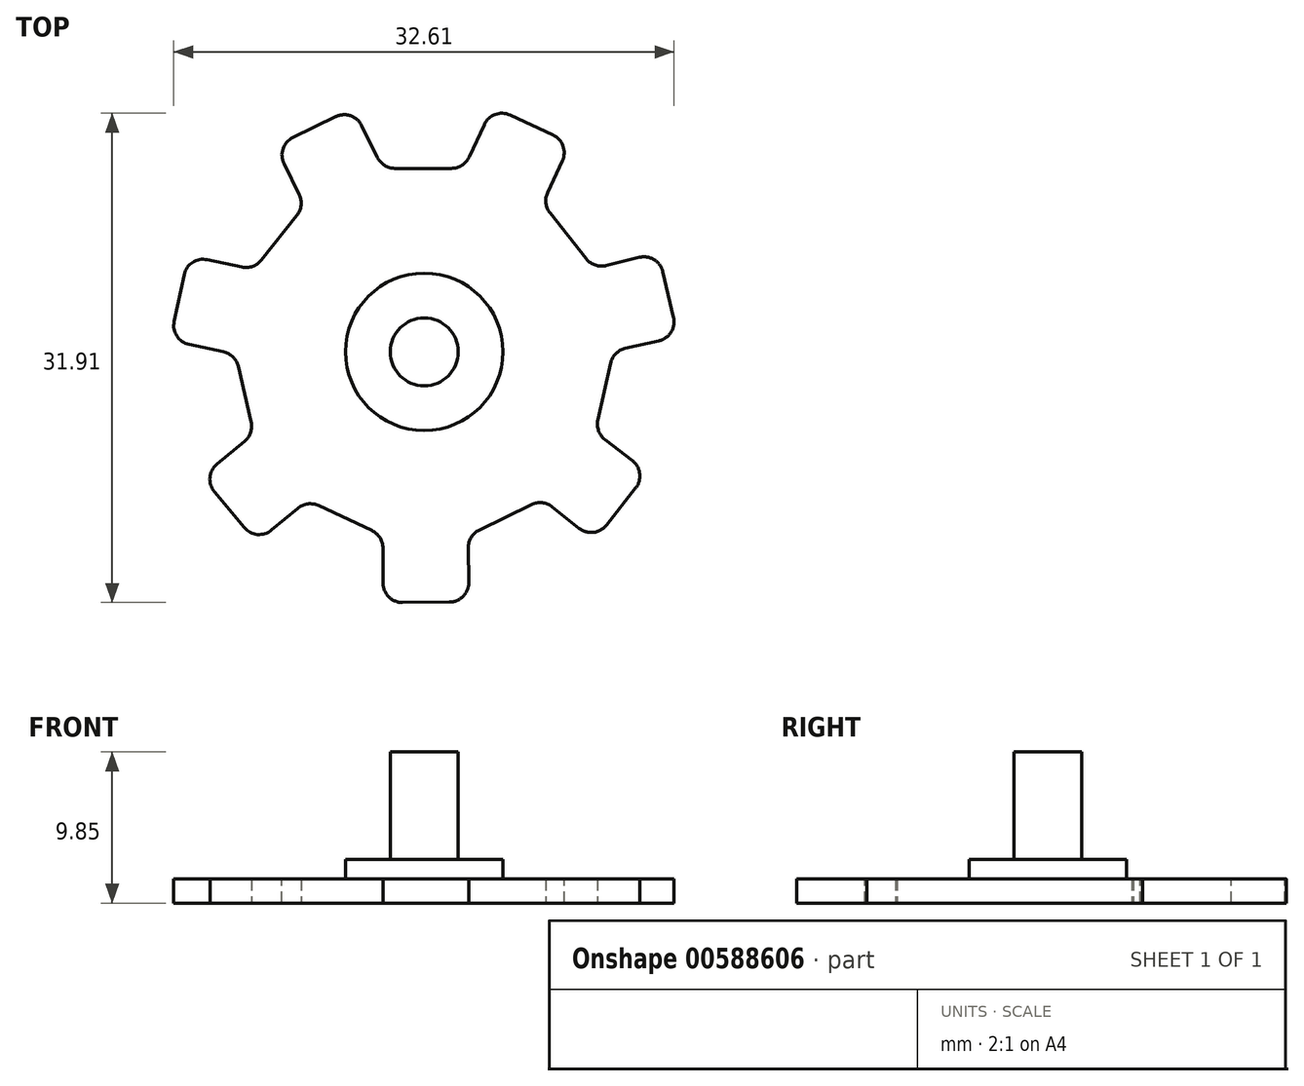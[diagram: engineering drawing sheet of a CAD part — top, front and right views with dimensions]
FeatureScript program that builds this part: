
annotation { "Feature Type Name" : "Feature", "Feature Type Description" : "" }
export const myFeature = defineFeature(function(context is Context, id is Id, definition is map)
    precondition{}
    {
        {
            var Q0;
            Q0=qCreatedBy(makeId("Top.planeOp"),FACE);
            var sketch = newSketch(context, id + "F0", { "sketchPlane" : qUnion([Q0])});
            skLineSegment(sketch, "E0", {"start": v(-2.4, 14.6) * mm, "end": v(-2.4, 10.7) * mm});
            skLineSegment(sketch, "E1", {"start": v(-2.4, 10.7) * mm, "end": v(-6.8, 8.65) * mm});
            skLineSegment(sketch, "E2", {"start": v(-6.8, 8.65) * mm, "end": v(-9.75, 11.1) * mm});
            skLineSegment(sketch, "E3", {"start": v(-9.75, 11.1) * mm, "end": v(-12.94, 7.27) * mm});
            skLineSegment(sketch, "E4", {"start": v(-12.94, 7.27) * mm, "end": v(-9.92, 4.76) * mm});
            skLineSegment(sketch, "E5", {"start": v(-9.92, 4.76) * mm, "end": v(-10.99, 0.15) * mm});
            skLineSegment(sketch, "E6", {"start": v(-10.99, 0.15) * mm, "end": v(-14.79, -0.67) * mm});
            skLineSegment(sketch, "E7", {"start": v(-14.79, -0.67) * mm, "end": v(-13.73, -5.6) * mm});
            skLineSegment(sketch, "E8", {"start": v(-13.73, -5.6) * mm, "end": v(-9.92, -4.78) * mm});
            skLineSegment(sketch, "E9", {"start": v(-9.92, -4.78) * mm, "end": v(-6.97, -8.51) * mm});
            skLineSegment(sketch, "E10", {"start": v(-6.97, -8.51) * mm, "end": v(-8.66, -11.97) * mm});
            skLineSegment(sketch, "E11", {"start": v(-8.66, -11.97) * mm, "end": v(-4.14, -14.2) * mm});
            skLineSegment(sketch, "E12", {"start": v(-4.14, -14.2) * mm, "end": v(-2.42, -10.68) * mm});
            skLineSegment(sketch, "E13", {"start": v(-2.42, -10.68) * mm, "end": v(2.3, -10.68) * mm});
            skLineSegment(sketch, "E14", {"start": v(2.3, -10.68) * mm, "end": v(3.97, -14.26) * mm});
            skLineSegment(sketch, "E15", {"start": v(3.97, -14.26) * mm, "end": v(8.52, -12.15) * mm});
            skLineSegment(sketch, "E16", {"start": v(8.52, -12.15) * mm, "end": v(6.88, -8.63) * mm});
            skLineSegment(sketch, "E17", {"start": v(6.88, -8.63) * mm, "end": v(9.89, -4.84) * mm});
            skLineSegment(sketch, "E18", {"start": v(9.89, -4.84) * mm, "end": v(13.62, -5.78) * mm});
            skLineSegment(sketch, "E19", {"start": v(13.62, -5.78) * mm, "end": v(14.77, -0.9) * mm});
            skLineSegment(sketch, "E20", {"start": v(14.77, -0.9) * mm, "end": v(11, -0.04) * mm});
            skLineSegment(sketch, "E21", {"start": v(11, -0.04) * mm, "end": v(9.95, 4.67) * mm});
            skLineSegment(sketch, "E22", {"start": v(9.95, 4.67) * mm, "end": v(13, 7.03) * mm});
            skLineSegment(sketch, "E23", {"start": v(13, 7.03) * mm, "end": v(9.9, 10.98) * mm});
            skLineSegment(sketch, "E24", {"start": v(9.9, 10.98) * mm, "end": v(6.88, 8.58) * mm});
            skLineSegment(sketch, "E25", {"start": v(6.88, 8.58) * mm, "end": v(2.55, 10.7) * mm});
            skLineSegment(sketch, "E26", {"start": v(2.55, 10.7) * mm, "end": v(2.6, 14.56) * mm});
            skLineSegment(sketch, "E27", {"start": v(2.6, 14.56) * mm, "end": v(-2.4, 14.6) * mm});
            skSolve(sketch);
        }
        {
            var Q0;
            Q0=qSketchRegion(id+"F0",true);
            extrude(context, id + "F1", {"entities" : qUnion([Q0]), "depth" : 2.54 * mm, "offsetDistance" : 25.4 * mm});
        }
        {
            var Q0;
            Q0=makeQuery(id+"F1.opExtrude","SWEPT_BODY",BODY,{"disambiguationData":[OSD([sQuery(id+"F0.wireOp",EDGE,"E0"),sQuery(id+"F0.wireOp",EDGE,"E1"),sQuery(id+"F0.wireOp",EDGE,"E2"),sQuery(id+"F0.wireOp",EDGE,"E3"),sQuery(id+"F0.wireOp",EDGE,"E4"),sQuery(id+"F0.wireOp",EDGE,"E5"),sQuery(id+"F0.wireOp",EDGE,"E6"),sQuery(id+"F0.wireOp",EDGE,"E7"),sQuery(id+"F0.wireOp",EDGE,"E8"),sQuery(id+"F0.wireOp",EDGE,"E9"),sQuery(id+"F0.wireOp",EDGE,"E10"),sQuery(id+"F0.wireOp",EDGE,"E11"),sQuery(id+"F0.wireOp",EDGE,"E12"),sQuery(id+"F0.wireOp",EDGE,"E13"),sQuery(id+"F0.wireOp",EDGE,"E14"),sQuery(id+"F0.wireOp",EDGE,"E15"),sQuery(id+"F0.wireOp",EDGE,"E16"),sQuery(id+"F0.wireOp",EDGE,"E17"),sQuery(id+"F0.wireOp",EDGE,"E18"),sQuery(id+"F0.wireOp",EDGE,"E19"),sQuery(id+"F0.wireOp",EDGE,"E20"),sQuery(id+"F0.wireOp",EDGE,"E21"),sQuery(id+"F0.wireOp",EDGE,"E22"),sQuery(id+"F0.wireOp",EDGE,"E23"),sQuery(id+"F0.wireOp",EDGE,"E24"),sQuery(id+"F0.wireOp",EDGE,"E25"),sQuery(id+"F0.wireOp",EDGE,"E26"),sQuery(id+"F0.wireOp",EDGE,"E27")])]});
            var Q1;
            Q1=qCreatedBy(makeId("Origin.pointOp"),VERTEX);
            transform(context, id + "F2", {"entities" : qUnion([Q0]), "transformType" : TransformType.SCALE_UNIFORMLY, "scale" : 1.12, "scalePoint" : qUnion([Q1]), "makeCopy" : false});
        }
        {
            var Q0;
            Q0=makeQuery(id+"F1.opExtrude","SWEPT_EDGE",EDGE,{"disambiguationData":[OSD([sQuery(id+"F0.wireOp",EDGE,"E6"),sQuery(id+"F0.wireOp",EDGE,"E7")])]});
            var Q1;
            Q1=makeQuery(id+"F1.opExtrude","SWEPT_EDGE",EDGE,{"disambiguationData":[OSD([sQuery(id+"F0.wireOp",EDGE,"E5"),sQuery(id+"F0.wireOp",EDGE,"E6")])]});
            var Q2;
            {var subQ0=sQuery(id+"F0.wireOp",EDGE,"E4");Q2=makeQuery(id+"Fj5wciNK8VLjmr4_1.opFillet","BLEND_EDGE",EDGE,{"blendedFrom":[makeQuery(id+"F1.opExtrude","CAP_EDGE",EDGE,{"disambiguationData":[OSD([subQ0])],"isStart":false}),makeQuery(id+"F1.opExtrude","SWEPT_FACE",FACE,{"disambiguationData":[OSD([subQ0])]})],"blendedInto":[makeQuery(id+"F1.opExtrude","SWEPT_FACE",FACE,{"disambiguationData":[OSD([subQ0])]})]});}
            var Q3;
            Q3=makeQuery(id+"F1.opExtrude","SWEPT_EDGE",EDGE,{"disambiguationData":[OSD([sQuery(id+"F0.wireOp",EDGE,"E3"),sQuery(id+"F0.wireOp",EDGE,"E4")])]});
            var Q4;
            Q4=makeQuery(id+"F1.opExtrude","SWEPT_EDGE",EDGE,{"disambiguationData":[OSD([sQuery(id+"F0.wireOp",EDGE,"E2"),sQuery(id+"F0.wireOp",EDGE,"E3")])]});
            var Q5;
            Q5=makeQuery(id+"F1.opExtrude","SWEPT_EDGE",EDGE,{"disambiguationData":[OSD([sQuery(id+"F0.wireOp",EDGE,"E1"),sQuery(id+"F0.wireOp",EDGE,"E2")])]});
            var Q6;
            Q6=makeQuery(id+"F1.opExtrude","SWEPT_EDGE",EDGE,{"disambiguationData":[OSD([sQuery(id+"F0.wireOp",EDGE,"E0"),sQuery(id+"F0.wireOp",EDGE,"E1")])]});
            var Q7;
            Q7=makeQuery(id+"F1.opExtrude","SWEPT_EDGE",EDGE,{"disambiguationData":[OSD([sQuery(id+"F0.wireOp",EDGE,"E0"),sQuery(id+"F0.wireOp",EDGE,"E27")])]});
            var Q8;
            Q8=makeQuery(id+"F1.opExtrude","SWEPT_EDGE",EDGE,{"disambiguationData":[OSD([sQuery(id+"F0.wireOp",EDGE,"E26"),sQuery(id+"F0.wireOp",EDGE,"E27")])]});
            var Q9;
            Q9=makeQuery(id+"F1.opExtrude","SWEPT_EDGE",EDGE,{"disambiguationData":[OSD([sQuery(id+"F0.wireOp",EDGE,"E25"),sQuery(id+"F0.wireOp",EDGE,"E26")])]});
            var Q10;
            Q10=makeQuery(id+"F1.opExtrude","SWEPT_EDGE",EDGE,{"disambiguationData":[OSD([sQuery(id+"F0.wireOp",EDGE,"E24"),sQuery(id+"F0.wireOp",EDGE,"E25")])]});
            var Q11;
            Q11=makeQuery(id+"F1.opExtrude","SWEPT_EDGE",EDGE,{"disambiguationData":[OSD([sQuery(id+"F0.wireOp",EDGE,"E23"),sQuery(id+"F0.wireOp",EDGE,"E24")])]});
            var Q12;
            Q12=makeQuery(id+"F1.opExtrude","SWEPT_EDGE",EDGE,{"disambiguationData":[OSD([sQuery(id+"F0.wireOp",EDGE,"E22"),sQuery(id+"F0.wireOp",EDGE,"E23")])]});
            var Q13;
            Q13=makeQuery(id+"F1.opExtrude","SWEPT_EDGE",EDGE,{"disambiguationData":[OSD([sQuery(id+"F0.wireOp",EDGE,"E21"),sQuery(id+"F0.wireOp",EDGE,"E22")])]});
            var Q14;
            Q14=makeQuery(id+"F1.opExtrude","SWEPT_EDGE",EDGE,{"disambiguationData":[OSD([sQuery(id+"F0.wireOp",EDGE,"E20"),sQuery(id+"F0.wireOp",EDGE,"E21")])]});
            var Q15;
            Q15=makeQuery(id+"F1.opExtrude","SWEPT_EDGE",EDGE,{"disambiguationData":[OSD([sQuery(id+"F0.wireOp",EDGE,"E19"),sQuery(id+"F0.wireOp",EDGE,"E20")])]});
            var Q16;
            Q16=makeQuery(id+"F1.opExtrude","SWEPT_EDGE",EDGE,{"disambiguationData":[OSD([sQuery(id+"F0.wireOp",EDGE,"E18"),sQuery(id+"F0.wireOp",EDGE,"E19")])]});
            var Q17;
            Q17=makeQuery(id+"F1.opExtrude","SWEPT_EDGE",EDGE,{"disambiguationData":[OSD([sQuery(id+"F0.wireOp",EDGE,"E17"),sQuery(id+"F0.wireOp",EDGE,"E18")])]});
            var Q18;
            Q18=makeQuery(id+"F1.opExtrude","SWEPT_EDGE",EDGE,{"disambiguationData":[OSD([sQuery(id+"F0.wireOp",EDGE,"E16"),sQuery(id+"F0.wireOp",EDGE,"E17")])]});
            var Q19;
            Q19=makeQuery(id+"F1.opExtrude","SWEPT_EDGE",EDGE,{"disambiguationData":[OSD([sQuery(id+"F0.wireOp",EDGE,"E15"),sQuery(id+"F0.wireOp",EDGE,"E16")])]});
            var Q20;
            Q20=makeQuery(id+"F1.opExtrude","SWEPT_EDGE",EDGE,{"disambiguationData":[OSD([sQuery(id+"F0.wireOp",EDGE,"E14"),sQuery(id+"F0.wireOp",EDGE,"E15")])]});
            var Q21;
            Q21=makeQuery(id+"F1.opExtrude","SWEPT_EDGE",EDGE,{"disambiguationData":[OSD([sQuery(id+"F0.wireOp",EDGE,"E13"),sQuery(id+"F0.wireOp",EDGE,"E14")])]});
            var Q22;
            Q22=makeQuery(id+"F1.opExtrude","SWEPT_EDGE",EDGE,{"disambiguationData":[OSD([sQuery(id+"F0.wireOp",EDGE,"E12"),sQuery(id+"F0.wireOp",EDGE,"E13")])]});
            var Q23;
            Q23=makeQuery(id+"F1.opExtrude","SWEPT_EDGE",EDGE,{"disambiguationData":[OSD([sQuery(id+"F0.wireOp",EDGE,"E11"),sQuery(id+"F0.wireOp",EDGE,"E12")])]});
            var Q24;
            Q24=makeQuery(id+"F1.opExtrude","SWEPT_EDGE",EDGE,{"disambiguationData":[OSD([sQuery(id+"F0.wireOp",EDGE,"E10"),sQuery(id+"F0.wireOp",EDGE,"E11")])]});
            var Q25;
            Q25=makeQuery(id+"F1.opExtrude","SWEPT_EDGE",EDGE,{"disambiguationData":[OSD([sQuery(id+"F0.wireOp",EDGE,"E9"),sQuery(id+"F0.wireOp",EDGE,"E10")])]});
            var Q26;
            Q26=makeQuery(id+"F1.opExtrude","SWEPT_EDGE",EDGE,{"disambiguationData":[OSD([sQuery(id+"F0.wireOp",EDGE,"E8"),sQuery(id+"F0.wireOp",EDGE,"E9")])]});
            var Q27;
            Q27=makeQuery(id+"F1.opExtrude","SWEPT_EDGE",EDGE,{"disambiguationData":[OSD([sQuery(id+"F0.wireOp",EDGE,"E7"),sQuery(id+"F0.wireOp",EDGE,"E8")])]});
            var Q28;
            Q28=makeQuery(id+"F1.opExtrude","SWEPT_EDGE",EDGE,{"disambiguationData":[OSD([sQuery(id+"F0.wireOp",EDGE,"E4"),sQuery(id+"F0.wireOp",EDGE,"E5")])]});
            fillet(context, id + "F3", {"entities" : qUnion([Q0, Q1, Q2, Q3, Q4, Q5, Q6, Q7, Q8, Q9, Q10, Q11, Q12, Q13, Q14, Q15, Q16, Q17, Q18, Q19, Q20, Q21, Q22, Q23, Q24, Q25, Q26, Q27, Q28]), "radius" : 1.27 * mm, "tangentPropagation" : true, "allowEdgeOverflow" : false});
        }
        {
            var Q0;
            Q0=makeQuery(id+"F0.imprint","IMPRINT",FACE,{"disambiguationData":[TD([[makeQuery(id+"F0.imprint","IMPRINT",EDGE,{"derivedFrom":sQuery(id+"F0.wireOp",EDGE,"E0")}),1.0]])]});
            var sketch = newSketch(context, id + "F4", { "sketchPlane" : qUnion([Q0])});
            skCircle(sketch, "E28", {"center": v(0, 0) * mm, "radius": 2.2 * mm});
            skPoint(sketch, "E29.start.orphan", {"position": v(0, -2.2) * mm});
            skSolve(sketch);
        }
        {
            var Q0;
            Q0 = qSketchRegion(id + "F4", true);
            extrude(context, id + "F5", {"entities" : qUnion([Q0]), "operationType" : NewBodyOperationType.ADD, "oppositeDirection" : true, "depth" : 7 * mm, "offsetDistance" : 25.4 * mm});
        }
        {
            var Q0;
            Q0=makeQuery(id+"F1.opExtrude","SWEPT_BODY",BODY,{"disambiguationData":[OSD([sQuery(id+"F0.wireOp",EDGE,"E0"),sQuery(id+"F0.wireOp",EDGE,"E1"),sQuery(id+"F0.wireOp",EDGE,"E2"),sQuery(id+"F0.wireOp",EDGE,"E3"),sQuery(id+"F0.wireOp",EDGE,"E4"),sQuery(id+"F0.wireOp",EDGE,"E5"),sQuery(id+"F0.wireOp",EDGE,"E6"),sQuery(id+"F0.wireOp",EDGE,"E7"),sQuery(id+"F0.wireOp",EDGE,"E8"),sQuery(id+"F0.wireOp",EDGE,"E9"),sQuery(id+"F0.wireOp",EDGE,"E10"),sQuery(id+"F0.wireOp",EDGE,"E11"),sQuery(id+"F0.wireOp",EDGE,"E12"),sQuery(id+"F0.wireOp",EDGE,"E13"),sQuery(id+"F0.wireOp",EDGE,"E14"),sQuery(id+"F0.wireOp",EDGE,"E15"),sQuery(id+"F0.wireOp",EDGE,"E16"),sQuery(id+"F0.wireOp",EDGE,"E17"),sQuery(id+"F0.wireOp",EDGE,"E18"),sQuery(id+"F0.wireOp",EDGE,"E19"),sQuery(id+"F0.wireOp",EDGE,"E20"),sQuery(id+"F0.wireOp",EDGE,"E21"),sQuery(id+"F0.wireOp",EDGE,"E22"),sQuery(id+"F0.wireOp",EDGE,"E23"),sQuery(id+"F0.wireOp",EDGE,"E24"),sQuery(id+"F0.wireOp",EDGE,"E25"),sQuery(id+"F0.wireOp",EDGE,"E26"),sQuery(id+"F0.wireOp",EDGE,"E27")])]});
            var Q1;
            Q1=makeQuery(id+"F1.opExtrude","CAP_EDGE",EDGE,{"disambiguationData":[OSD([sQuery(id+"F0.wireOp",EDGE,"E13")])],"isStart":true});
            transform(context, id + "F6", {"entities" : qUnion([Q0]), "transformType" : TransformType.ROTATION, "transformAxis" : qUnion([Q1]), "angle" : 180 * degree, "makeCopy" : false});
        }
        {
            var Q0;
            Q0=makeQuery(id+"F1.opExtrude","CAP_FACE",FACE,{"disambiguationData":[OSD([sQuery(id+"F0.wireOp",EDGE,"E0"),sQuery(id+"F0.wireOp",EDGE,"E1"),sQuery(id+"F0.wireOp",EDGE,"E2"),sQuery(id+"F0.wireOp",EDGE,"E3"),sQuery(id+"F0.wireOp",EDGE,"E4"),sQuery(id+"F0.wireOp",EDGE,"E5"),sQuery(id+"F0.wireOp",EDGE,"E6"),sQuery(id+"F0.wireOp",EDGE,"E7"),sQuery(id+"F0.wireOp",EDGE,"E8"),sQuery(id+"F0.wireOp",EDGE,"E9"),sQuery(id+"F0.wireOp",EDGE,"E10"),sQuery(id+"F0.wireOp",EDGE,"E11"),sQuery(id+"F0.wireOp",EDGE,"E12"),sQuery(id+"F0.wireOp",EDGE,"E13"),sQuery(id+"F0.wireOp",EDGE,"E14"),sQuery(id+"F0.wireOp",EDGE,"E15"),sQuery(id+"F0.wireOp",EDGE,"E16"),sQuery(id+"F0.wireOp",EDGE,"E17"),sQuery(id+"F0.wireOp",EDGE,"E18"),sQuery(id+"F0.wireOp",EDGE,"E19"),sQuery(id+"F0.wireOp",EDGE,"E20"),sQuery(id+"F0.wireOp",EDGE,"E21"),sQuery(id+"F0.wireOp",EDGE,"E22"),sQuery(id+"F0.wireOp",EDGE,"E23"),sQuery(id+"F0.wireOp",EDGE,"E24"),sQuery(id+"F0.wireOp",EDGE,"E25"),sQuery(id+"F0.wireOp",EDGE,"E26"),sQuery(id+"F0.wireOp",EDGE,"E27")])],"isStart":true});
            extrude(context, id + "F7", {"entities" : qUnion([Q0]), "operationType" : NewBodyOperationType.REMOVE, "oppositeDirection" : true, "depth" : 1.27 * mm, "offsetDistance" : 25.4 * mm});
        }
        {
            var Q0;
            Q0=makeQuery(id+"F7.boolean.opBoolean","COPY",FACE,{"derivedFrom":makeQuery(id+"F7.opExtrude","CAP_FACE",FACE,{"disambiguationData":[OSD([sQuery(id+"F0.wireOp",EDGE,"E0"),sQuery(id+"F0.wireOp",EDGE,"E1"),sQuery(id+"F0.wireOp",EDGE,"E2"),sQuery(id+"F0.wireOp",EDGE,"E3"),sQuery(id+"F0.wireOp",EDGE,"E4"),sQuery(id+"F0.wireOp",EDGE,"E5"),sQuery(id+"F0.wireOp",EDGE,"E6"),sQuery(id+"F0.wireOp",EDGE,"E7"),sQuery(id+"F0.wireOp",EDGE,"E8"),sQuery(id+"F0.wireOp",EDGE,"E9"),sQuery(id+"F0.wireOp",EDGE,"E10"),sQuery(id+"F0.wireOp",EDGE,"E11"),sQuery(id+"F0.wireOp",EDGE,"E12"),sQuery(id+"F0.wireOp",EDGE,"E13"),sQuery(id+"F0.wireOp",EDGE,"E14"),sQuery(id+"F0.wireOp",EDGE,"E15"),sQuery(id+"F0.wireOp",EDGE,"E16"),sQuery(id+"F0.wireOp",EDGE,"E17"),sQuery(id+"F0.wireOp",EDGE,"E18"),sQuery(id+"F0.wireOp",EDGE,"E19"),sQuery(id+"F0.wireOp",EDGE,"E20"),sQuery(id+"F0.wireOp",EDGE,"E21"),sQuery(id+"F0.wireOp",EDGE,"E22"),sQuery(id+"F0.wireOp",EDGE,"E23"),sQuery(id+"F0.wireOp",EDGE,"E24"),sQuery(id+"F0.wireOp",EDGE,"E25"),sQuery(id+"F0.wireOp",EDGE,"E26"),sQuery(id+"F0.wireOp",EDGE,"E27")])],"isStart":false})});
            var sketch = newSketch(context, id + "F8", { "sketchPlane" : qUnion([Q0])});
            skCircle(sketch, "E30.0", {"center": v(0, -23.93) * mm, "radius": 5.13 * mm});
            skLineSegment(sketch, "E31", {"start": v(-5.13, -23.93) * mm, "end": v(5.13, -23.93) * mm, "construction": true});
            skSolve(sketch);
        }
        {
            var Q0;
            Q0=makeQuery(id+"F8.imprint","IMPRINT",FACE,{"disambiguationData":[TD([[makeQuery(id+"F8.imprint","IMPRINT",EDGE,{"derivedFrom":sQuery(id+"F8.wireOp",EDGE,"E30.0")}),1.0]])]});
            extrude(context, id + "F9", {"entities" : qUnion([Q0]), "operationType" : NewBodyOperationType.ADD, "depth" : 1.27 * mm, "offsetDistance" : 25.4 * mm});
        }
    });
